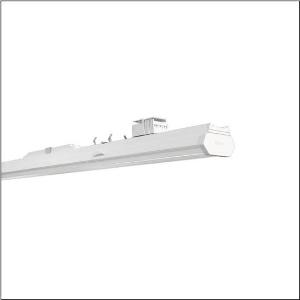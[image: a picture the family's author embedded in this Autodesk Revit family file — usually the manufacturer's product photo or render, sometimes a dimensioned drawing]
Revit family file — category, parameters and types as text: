
# Revit family: licross_r__21_protected_mo_52td1bvn465g_e1b8
name_source: partatom
category: Lighting Fixtures
units: mm (PartAtom-declared; Revit-internal decimal feet)

## family parameters
Cut with Voids When Loaded = No
Host = Face
Light Source = No
Part Type = Normal
Room Calculation Point = No
Round Connector Dimension = Use Diameter
Shared = No

## types (1)
- --- (1 x LED, 6500 lm, 39 W, 4000K)
    Apparent Load = 39 VA
    CIE Flux Codes = 54 82 95 97 100
    Color Rendering = 80
    Color Temperature = 4000K
    Default Elevation = 1800 mm
    Description = Licross® 21 Protected MO, luminaire insert, of sheet steel, galvanised, coil coated, white, length: 1.500mm, width: 90mm, height: 101mm, LED rated luminous flux: 6.500lm, light colour: 840, control gear: DALI 2, CLO, with plug, 5-pole, with phase selection, mains connection: 220..240V, AC, 50/60Hz, start of lifetime: 39W, end of service life: 46W, halogen-free wiring, primary optical cover: cover, of PMMA, light emission: direct distribution, primary light characteristic: symmetric, protection rating (complete): IP54, insulation class (complete): insulation class I (protective earthing), certification: CE, ENEC, VDE, UKCA, protection symbol: D if used in an environment with non-conductive dust loads with corresponding accessories, impact resistance: IK06, permissible ambient temperature for indoor applications: -25..+45°C, corresponds to IFS (International Featured Standards) requirements for safety and quality in the food industry, reducing of maximum allowable ambient temperature of 5°C with ceiling mounting, LABS conformity tested according to VDMA 24364:2018-05, packaging unit: 1 piece
    Height = 92 mm
    Lamp = 1 x LED
    Lamp Light Flux = 6500 lm
    Lamp Power = 39 W
    Lamp count = 1
    Length = 1500 mm
    Luminous efficacy = 167 lm/W
    Manufacturer = Siteco
    ModVariant = No
    Model = 52TD1BVN465G
    Mounting Place = Ceiling
    Mounting Type = Pendant
    Number of Poles = 1
    OnlyDefault = Yes
    Power Factor = 1
    Product Name = Licross® 21 Protected MO
    Product group = luminaire insert
    ProductGroupID = 901
    Protection Class = Protection class I
    Protection Degree = IP 54
    RLX_Detail_Level = 1
    RLX_Emergency_Light_Flux = 0 lm
    RLX_Emergency_Type = 0
    RLX_Emergency_Type_DB = No
    RlxData = <blob elided: 24373 chars, md5=8975ab9b>
    Socket = socket
    Standby Power = 0 W
    System Light Flux = 6500 lm
    System Power = 39 W
    Type Comments = factory setting: luminous flux: 100 % | dim-lin: 254 | 262 mA
    Type Image = l_1256148.jpg
    URL = http://relux.com
    VarID = @adj_035173
    Voltage = 0 V
    Weight = 0.00 kg
    Width = 88 mm

## geometry (parser evidence)
native form markers: Blend x4, Sweep x9
no freeform markers — native parametric forms only
